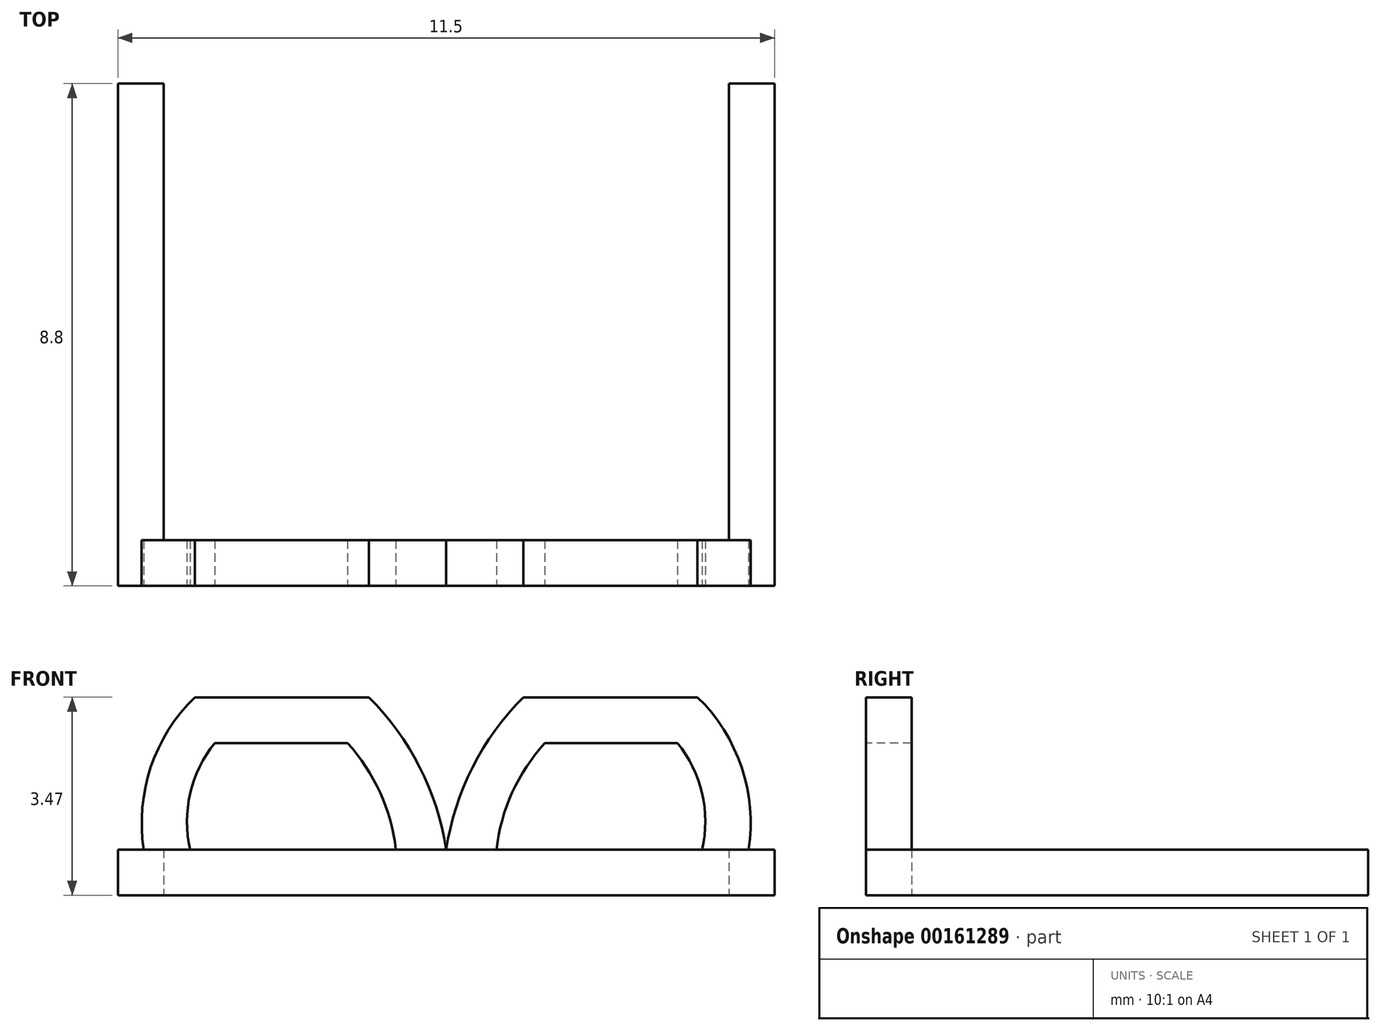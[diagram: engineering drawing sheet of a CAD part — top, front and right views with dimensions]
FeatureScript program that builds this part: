
annotation { "Feature Type Name" : "Feature", "Feature Type Description" : "" }
export const myFeature = defineFeature(function(context is Context, id is Id, definition is map)
    precondition{}
    {
        {
            var Q0;
            Q0=qCreatedBy(makeId("Top.planeOp"),FACE);
            var sketch = newSketch(context, id + "F0", { "sketchPlane" : qUnion([Q0])});
            skLineSegment(sketch, "E0.bottom", {"start": v(5.75, 4.4) * mm, "end": v(-5.75, 4.4) * mm});
            skLineSegment(sketch, "E0.top", {"start": v(5.75, -4.4) * mm, "end": v(-5.75, -4.4) * mm});
            skLineSegment(sketch, "E0.left", {"start": v(5.75, 4.4) * mm, "end": v(5.75, -4.4) * mm});
            skLineSegment(sketch, "E0.right", {"start": v(-5.75, 4.4) * mm, "end": v(-5.75, -4.4) * mm});
            skPoint(sketch, "E0.middle", {"position": v(0, 0) * mm});
            skLineSegment(sketch, "E1.bottom", {"start": v(-4.95, 4.4) * mm, "end": v(4.95, 4.4) * mm});
            skLineSegment(sketch, "E1.top", {"start": v(-4.95, -3.6) * mm, "end": v(4.95, -3.6) * mm});
            skLineSegment(sketch, "E1.left", {"start": v(-4.95, 4.4) * mm, "end": v(-4.95, -3.6) * mm});
            skLineSegment(sketch, "E1.right", {"start": v(4.95, 4.4) * mm, "end": v(4.95, -3.6) * mm});
            skSolve(sketch);
        }
        {
            var Q0;
            Q0=makeQuery(id+"F0.imprint","IMPRINT",FACE,{"disambiguationData":[TD([[makeQuery(id+"F0.imprint","IMPRINT",EDGE,{"derivedFrom":sQuery(id+"F0.wireOp",EDGE,"E0.top")}),-1.0]])]});
            extrude(context, id + "F1", {"entities" : qUnion([Q0]), "depth" : .8 * mm});
        }
        {
            var Q0;
            Q0=makeQuery(id+"F1.opExtrude","SWEPT_FACE",FACE,{"disambiguationData":[OSD([sQuery(id+"F0.wireOp",EDGE,"E0.top")])]});
            var sketch = newSketch(context, id + "F2", { "sketchPlane" : qUnion([Q0])});
            skArc(sketch, "E2", {"start": v(-4.4, 3.47) * mm, "mid": v(-5.17, 2.24) * mm, "end": v(-5.3, 0.8) * mm});
            skLineSegment(sketch, "E3", {"start": v(-4.4, 3.47) * mm, "end": v(-1.35, 3.47) * mm});
            skArc(sketch, "E4", {"start": v(0, 0.8) * mm, "mid": v(-0.46, 2.24) * mm, "end": v(-1.35, 3.47) * mm});
            skLineSegment(sketch, "E5", {"start": v(-4.05, 2.67) * mm, "end": v(-1.73, 2.67) * mm});
            skArc(sketch, "E6", {"start": v(-4.05, 2.67) * mm, "mid": v(-4.48, 1.78) * mm, "end": v(-4.48, 0.8) * mm});
            skArc(sketch, "E7", {"start": v(-0.88, 0.8) * mm, "mid": v(-1.16, 1.8) * mm, "end": v(-1.73, 2.67) * mm});
            skLineSegment(sketch, "E8.MirrorCS", {"start": v(4.4, 3.47) * mm, "end": v(1.35, 3.47) * mm});
            skArc(sketch, "E9.MirrorCS", {"start": v(4.05, 2.67) * mm, "mid": v(4.48, 1.78) * mm, "end": v(4.48, 0.8) * mm});
            skArc(sketch, "E10.MirrorCS", {"start": v(0.88, 0.8) * mm, "mid": v(1.16, 1.8) * mm, "end": v(1.73, 2.67) * mm});
            skArc(sketch, "E11.MirrorCS", {"start": v(0, 0.8) * mm, "mid": v(0.46, 2.24) * mm, "end": v(1.35, 3.47) * mm});
            skArc(sketch, "E12.MirrorCS", {"start": v(4.4, 3.47) * mm, "mid": v(5.17, 2.24) * mm, "end": v(5.3, 0.8) * mm});
            skLineSegment(sketch, "E13.MirrorCS", {"start": v(4.05, 2.67) * mm, "end": v(1.73, 2.67) * mm});
            skSolve(sketch);
        }
        {
            var Q0;
            {var subQ1=sQuery(id+"F2.wireOp",EDGE,"E2");Q0=makeQuery(id+"F2.imprint","IMPRINT",FACE,{"disambiguationData":[TD([[makeQuery(id+"F2.imprint","IMPRINT",EDGE,{"derivedFrom":subQ1}),1.0]])]});}
            var Q1;
            Q1=makeQuery(id+"F2.imprint","IMPRINT",FACE,{"disambiguationData":[TD([[makeQuery(id+"F2.imprint","IMPRINT",EDGE,{"derivedFrom":sQuery(id+"F2.wireOp",EDGE,"E8.MirrorCS")}),1.0]])]});
            extrude(context, id + "F3", {"entities" : qUnion([Q0, Q1]), "oppositeDirection" : true, "depth" : .8 * mm});
        }
    });
